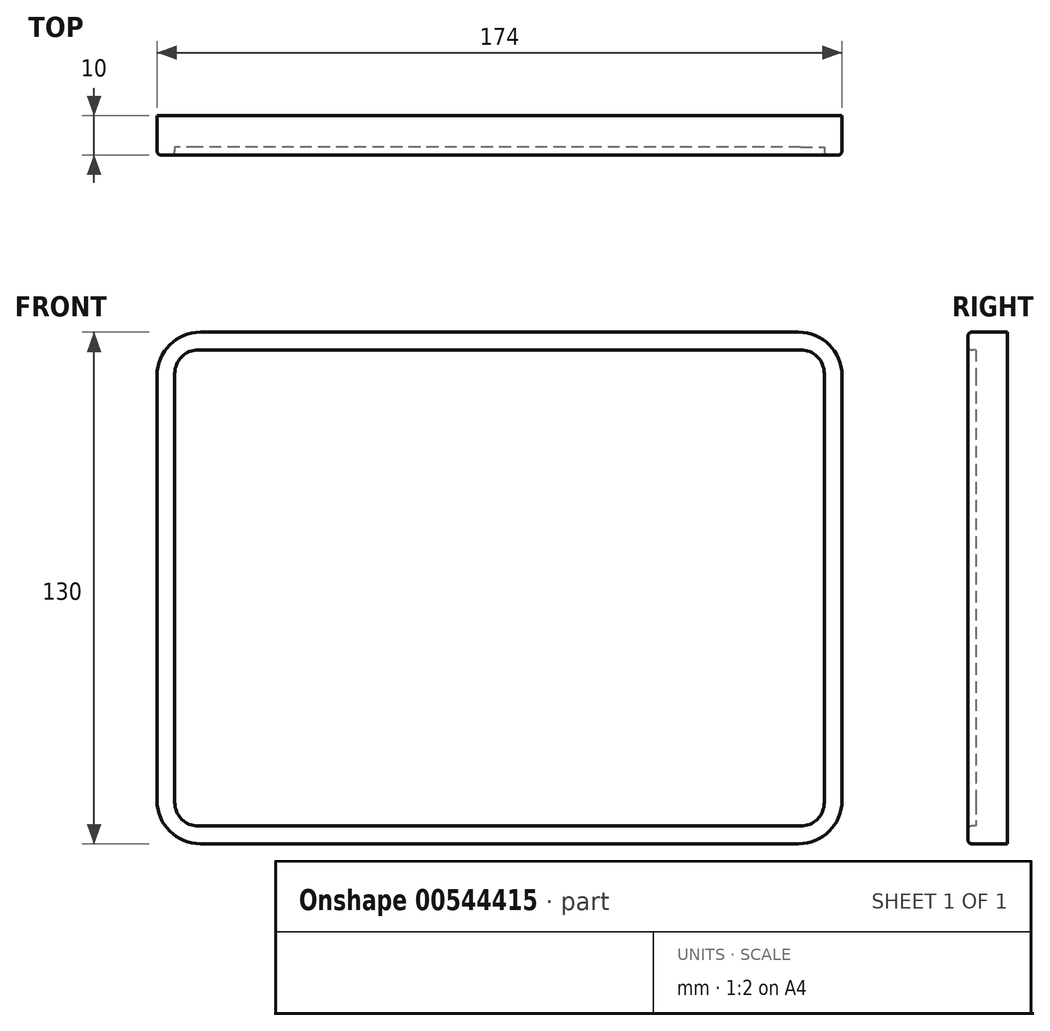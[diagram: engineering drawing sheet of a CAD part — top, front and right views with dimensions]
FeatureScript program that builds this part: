
annotation { "Feature Type Name" : "Feature", "Feature Type Description" : "" }
export const myFeature = defineFeature(function(context is Context, id is Id, definition is map)
    precondition{}
    {
        {
            var Q0;
            Q0=qCreatedBy(makeId("Front.planeOp"),FACE);
            var sketch = newSketch(context, id + "F0", { "sketchPlane" : qUnion([Q0])});
            skLineSegment(sketch, "E0.bottom", {"start": v(76, 65) * mm, "end": v(-76, 65) * mm});
            skLineSegment(sketch, "E0.top", {"start": v(76, -65) * mm, "end": v(-76, -65) * mm});
            skLineSegment(sketch, "E0.left", {"start": v(87, 54) * mm, "end": v(87, -54) * mm});
            skLineSegment(sketch, "E0.right", {"start": v(-87, 54) * mm, "end": v(-87, -54) * mm});
            skPoint(sketch, "E0.middle", {"position": v(0, 0) * mm});
            skPoint(sketch, "E1.visualSharp", {"position": v(87, 65) * mm});
            skArc(sketch, "E1.filletArc", {"start": v(87, 54) * mm, "mid": v(83.78, 61.78) * mm, "end": v(76, 65) * mm});
            skPoint(sketch, "E2.visualSharp", {"position": v(87, -65) * mm});
            skArc(sketch, "E2.filletArc", {"start": v(76, -65) * mm, "mid": v(83.78, -61.78) * mm, "end": v(87, -54) * mm});
            skPoint(sketch, "E3.visualSharp", {"position": v(-87, -65) * mm});
            skArc(sketch, "E3.filletArc", {"start": v(-87, -54) * mm, "mid": v(-83.78, -61.78) * mm, "end": v(-76, -65) * mm});
            skPoint(sketch, "E4.visualSharp", {"position": v(-87, 65) * mm});
            skArc(sketch, "E4.filletArc", {"start": v(-76, 65) * mm, "mid": v(-83.78, 61.78) * mm, "end": v(-87, 54) * mm});
            skLineSegment(sketch, "E5.0", {"start": v(76.5, 60.5) * mm, "end": v(-76.5, 60.5) * mm});
            skLineSegment(sketch, "E6.0", {"start": v(-82.5, 54.5) * mm, "end": v(-82.5, -54.5) * mm});
            skLineSegment(sketch, "E7.0", {"start": v(82.5, 54.5) * mm, "end": v(82.5, -54.5) * mm});
            skLineSegment(sketch, "E8.0", {"start": v(76.5, -60.5) * mm, "end": v(-76.5, -60.5) * mm});
            skPoint(sketch, "E9.visualSharp", {"position": v(-82.5, 60.5) * mm});
            skArc(sketch, "E9.filletArc", {"start": v(-76.5, 60.5) * mm, "mid": v(-80.74, 58.74) * mm, "end": v(-82.5, 54.5) * mm});
            skPoint(sketch, "E10.visualSharp", {"position": v(82.5, 60.5) * mm});
            skArc(sketch, "E10.filletArc", {"start": v(82.5, 54.5) * mm, "mid": v(80.74, 58.74) * mm, "end": v(76.5, 60.5) * mm});
            skPoint(sketch, "E11.visualSharp", {"position": v(-82.5, -60.5) * mm});
            skArc(sketch, "E11.filletArc", {"start": v(-82.5, -54.5) * mm, "mid": v(-80.74, -58.74) * mm, "end": v(-76.5, -60.5) * mm});
            skPoint(sketch, "E12.visualSharp", {"position": v(82.5, -60.5) * mm});
            skArc(sketch, "E12.filletArc", {"start": v(76.5, -60.5) * mm, "mid": v(80.74, -58.74) * mm, "end": v(82.5, -54.5) * mm});
            skSolve(sketch);
        }
        {
            var Q0;
            Q0 = qSketchRegion(id + "F0", true);
            var Q1;
            Q1=makeQuery(id+"F0.imprint","IMPRINT",FACE,{"disambiguationData":[TD([[makeQuery(id+"F0.imprint","IMPRINT",EDGE,{"derivedFrom":sQuery(id+"F0.wireOp",EDGE,"E5.0")}),1.0]])]});
            extrude(context, id + "F1", {"entities" : qUnion([Q0, Q1]), "depth" : 10 * mm, "offsetDistance" : 25 * mm});
        }
        {
            var Q0;
            Q0=makeQuery(id+"F1.opExtrude","CAP_FACE",FACE,{"disambiguationData":[OSD([sQuery(id+"F0.wireOp",EDGE,"E0.bottom"),sQuery(id+"F0.wireOp",EDGE,"E0.top"),sQuery(id+"F0.wireOp",EDGE,"E0.left"),sQuery(id+"F0.wireOp",EDGE,"E0.right"),sQuery(id+"F0.wireOp",EDGE,"E1.filletArc"),sQuery(id+"F0.wireOp",EDGE,"E2.filletArc"),sQuery(id+"F0.wireOp",EDGE,"E3.filletArc"),sQuery(id+"F0.wireOp",EDGE,"E4.filletArc")])],"isStart":false});
            var sketch = newSketch(context, id + "F2", { "sketchPlane" : qUnion([Q0])});
            skArc(sketch, "E13.0", {"start": v(-76.5, 60.5) * mm, "mid": v(-80.74, 58.74) * mm, "end": v(-82.5, 54.5) * mm});
            skLineSegment(sketch, "E14.0", {"start": v(76.5, 60.5) * mm, "end": v(-76.5, 60.5) * mm});
            skArc(sketch, "E15.0", {"start": v(82.5, 54.5) * mm, "mid": v(80.74, 58.74) * mm, "end": v(76.5, 60.5) * mm});
            skLineSegment(sketch, "E16.0", {"start": v(82.5, 54.5) * mm, "end": v(82.5, -54.5) * mm});
            skArc(sketch, "E17.0", {"start": v(76.5, -60.5) * mm, "mid": v(80.74, -58.74) * mm, "end": v(82.5, -54.5) * mm});
            skLineSegment(sketch, "E17.1", {"start": v(76.5, -60.5) * mm, "end": v(-76.5, -60.5) * mm});
            skArc(sketch, "E17.2", {"start": v(-82.5, -54.5) * mm, "mid": v(-80.74, -58.74) * mm, "end": v(-76.5, -60.5) * mm});
            skLineSegment(sketch, "E17.3", {"start": v(-82.5, 54.5) * mm, "end": v(-82.5, -54.5) * mm});
            skSolve(sketch);
        }
        {
            var Q0;
            Q0 = qSketchRegion(id + "F2", true);
            extrude(context, id + "F3", {"entities" : qUnion([Q0]), "operationType" : NewBodyOperationType.REMOVE, "oppositeDirection" : true, "depth" : 2 * mm, "offsetDistance" : 25 * mm});
        }
        {
            var Q0;
            Q0=makeQuery(id+"F1.opExtrude","CAP_FACE",FACE,{"disambiguationData":[OSD([sQuery(id+"F0.wireOp",EDGE,"E0.bottom"),sQuery(id+"F0.wireOp",EDGE,"E0.top"),sQuery(id+"F0.wireOp",EDGE,"E0.left"),sQuery(id+"F0.wireOp",EDGE,"E0.right"),sQuery(id+"F0.wireOp",EDGE,"E1.filletArc"),sQuery(id+"F0.wireOp",EDGE,"E2.filletArc"),sQuery(id+"F0.wireOp",EDGE,"E3.filletArc"),sQuery(id+"F0.wireOp",EDGE,"E4.filletArc")])],"isStart":false});
            fillet(context, id + "F4", {"entities" : qUnion([Q0]), "radius" : 1 * mm, "tangentPropagation" : true, "allowEdgeOverflow" : false});
        }
    });
